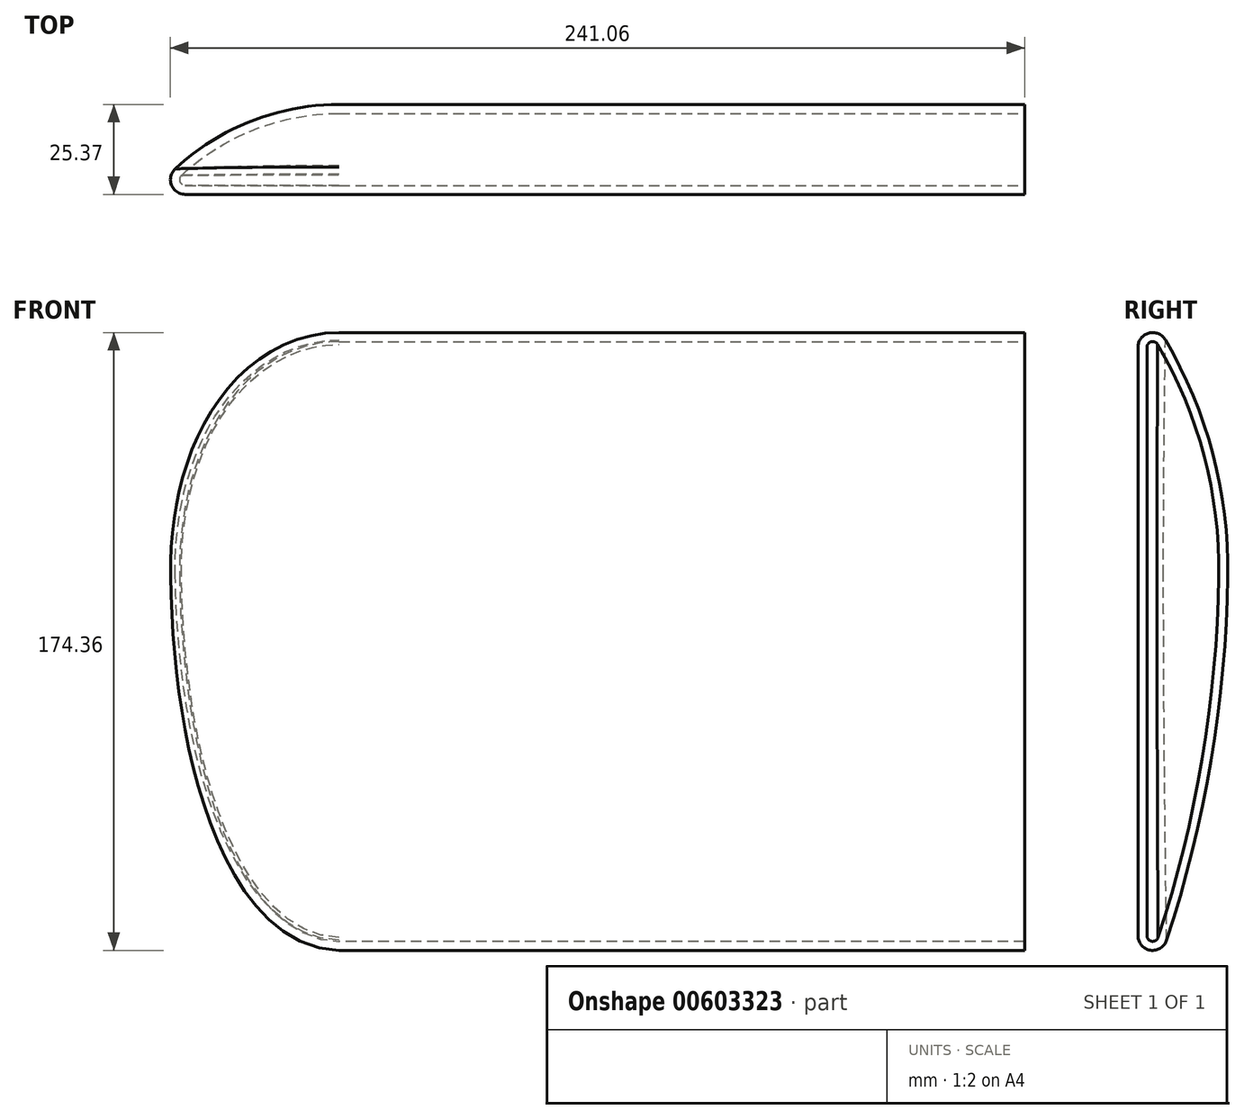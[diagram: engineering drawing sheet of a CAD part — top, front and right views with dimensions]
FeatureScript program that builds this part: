
annotation { "Feature Type Name" : "Feature", "Feature Type Description" : "" }
export const myFeature = defineFeature(function(context is Context, id is Id, definition is map)
    precondition{}
    {
        {
            var Q0;
            Q0=qCreatedBy(makeId("Front.planeOp"),FACE);
            var sketch = newSketch(context, id + "F0", { "sketchPlane" : qUnion([Q0])});
            skLineSegment(sketch, "E0.bottom", {"start": v(35.16, 65.27) * mm, "end": v(-168.9, 65.27) * mm});
            skLineSegment(sketch, "E0.top", {"start": v(35.16, -99.73) * mm, "end": v(-168.9, -99.73) * mm});
            skLineSegment(sketch, "E0.left", {"start": v(35.16, 65.27) * mm, "end": v(35.16, -99.73) * mm});
            skLineSegment(sketch, "E0.right", {"start": v(-168.9, 65.27) * mm, "end": v(-168.9, -99.73) * mm});
            skLineSegment(sketch, "E1.bottom", {"start": v(35.16, 65.27) * mm, "end": v(-226.34, 65.27) * mm});
            skLineSegment(sketch, "E1.top", {"start": v(35.16, -137.93) * mm, "end": v(-226.34, -137.93) * mm});
            skLineSegment(sketch, "E1.left", {"start": v(35.16, 65.27) * mm, "end": v(35.16, -137.93) * mm});
            skLineSegment(sketch, "E1.right", {"start": v(-226.34, 65.27) * mm, "end": v(-226.34, -137.93) * mm});
            skSolve(sketch);
        }
        {
            var Q0;
            {var subQ4=sQuery(id+"F0.wireOp",EDGE,"E0.top");Q0=makeQuery(id+"F0.imprint","IMPRINT",FACE,{"disambiguationData":[TD([[makeQuery(id+"F0.imprint","IMPRINT",EDGE,{"derivedFrom":subQ4}),1.0]])]});}
            extrude(context, id + "F1", {"entities" : qUnion([Q0]), "depth" : 25.4 * mm, "offsetDistance" : 25.4 * mm});
        }
        {
            var Q0;
            Q0=makeQuery(id+"F1.opExtrude","CAP_EDGE",EDGE,{"disambiguationData":[OSD([sQuery(id+"F0.wireOp",EDGE,"E1.bottom")])],"isStart":false});
            fillet(context, id + "F2", {"entities" : qUnion([Q0]), "radius" : 12.88 * mm, "tangentPropagation" : true, "allowEdgeOverflow" : false});
        }
        {
            var Q0;
            Q0=makeQuery(id+"F1.opExtrude","CAP_EDGE",EDGE,{"disambiguationData":[OSD([sQuery(id+"F0.wireOp",EDGE,"E1.bottom")])],"isStart":true});
            fillet(context, id + "F3", {"entities" : qUnion([Q0]), "radius" : 5.08 * mm, "tangentPropagation" : true, "allowEdgeOverflow" : false});
        }
        {
            var Q0;
            Q0=makeQuery(id+"F1.opExtrude","CAP_EDGE",EDGE,{"disambiguationData":[OSD([sQuery(id+"F0.wireOp",EDGE,"E1.right")])],"isStart":true});
            fillet(context, id + "F4", {"entities" : qUnion([Q0]), "radius" : 5.08 * mm, "tangentPropagation" : true, "allowEdgeOverflow" : false});
        }
        {
            var Q0;
            Q0=makeQuery(id+"F1.opExtrude","CAP_EDGE",EDGE,{"disambiguationData":[OSD([sQuery(id+"F0.wireOp",EDGE,"E0.top")])],"isStart":true});
            fillet(context, id + "F5", {"entities" : qUnion([Q0]), "radius" : 5.08 * mm, "tangentPropagation" : true, "allowEdgeOverflow" : false});
        }
        {
            var Q0;
            Q0=makeQuery(id+"F1.opExtrude","CAP_EDGE",EDGE,{"disambiguationData":[OSD([sQuery(id+"F0.wireOp",EDGE,"E0.top")])],"isStart":false});
            fillet(context, id + "F6", {"entities" : qUnion([Q0]), "radius" : 34.95 * mm, "tangentPropagation" : true, "allowEdgeOverflow" : false});
        }
        {
            var Q0;
            Q0 = qSketchRegion(id + "F0", true);
            extrude(context, id + "F7", {"entities" : qUnion([Q0]), "operationType" : NewBodyOperationType.ADD, "depth" : 25.4 * mm, "offsetDistance" : 25.4 * mm});
        }
        {
            var Q0;
            {var subQ0=sQuery(id+"F0.wireOp",EDGE,"E1.top");Q0=makeQuery(id+"F7.boolean.opBoolean","MERGE",EDGE,{"derivedFrom":[makeQuery(id+"F1.opExtrude","CAP_EDGE",EDGE,{"disambiguationData":[OSD([subQ0])],"isStart":true}),makeQuery(id+"F7.opExtrude","CAP_EDGE",EDGE,{"disambiguationData":[OSD([subQ0])],"isStart":true})]});}
            fillet(context, id + "F8", {"entities" : qUnion([Q0]), "radius" : 345.24 * mm, "tangentPropagation" : true, "allowEdgeOverflow" : false});
        }
        {
            var Q0;
            Q0=makeQuery(id+"F7.opExtrude","CAP_EDGE",EDGE,{"disambiguationData":[OSD([sQuery(id+"F0.wireOp",EDGE,"E1.bottom")])],"isStart":true});
            fillet(context, id + "F9", {"entities" : qUnion([Q0]), "radius" : 128.16 * mm, "tangentPropagation" : true, "allowEdgeOverflow" : false});
        }
        {
            var Q0;
            {var subQ0=sQuery(id+"F0.wireOp",EDGE,"E1.right");Q0=makeQuery(id+"F9.opFillet","BLEND_EDGE",EDGE,{"blendedFrom":[makeQuery(id+"F7.opExtrude","CAP_EDGE",EDGE,{"disambiguationData":[OSD([sQuery(id+"F0.wireOp",EDGE,"E1.bottom")])],"isStart":true}),makeQuery(id+"F7.boolean.opBoolean","MERGE",FACE,{"derivedFrom":[makeQuery(id+"F1.opExtrude","SWEPT_FACE",FACE,{"disambiguationData":[OSD([subQ0])]}),makeQuery(id+"F7.opExtrude","SWEPT_FACE",FACE,{"disambiguationData":[OSD([subQ0])]})]})],"blendedInto":[makeQuery(id+"F7.boolean.opBoolean","MERGE",FACE,{"derivedFrom":[makeQuery(id+"F1.opExtrude","SWEPT_FACE",FACE,{"disambiguationData":[OSD([subQ0])]}),makeQuery(id+"F7.opExtrude","SWEPT_FACE",FACE,{"disambiguationData":[OSD([subQ0])]})]})]});}
            fillet(context, id + "F10", {"entities" : qUnion([Q0]), "radius" : 68.07 * mm, "tangentPropagation" : true, "allowEdgeOverflow" : false});
        }
        {
            var Q0;
            {var subQ0=sQuery(id+"F0.wireOp",EDGE,"E1.right");var subQ1=sQuery(id+"F0.wireOp",EDGE,"E1.left");var subQ2=sQuery(id+"F0.wireOp",EDGE,"E1.top");var subQ3=sQuery(id+"F0.wireOp",EDGE,"E1.bottom");Q0=makeQuery(id+"F10.opFillet","BLEND_EDGE",EDGE,{"blendedFrom":[makeQuery(id+"F9.opFillet","BLEND_EDGE",EDGE,{"blendedFrom":[makeQuery(id+"F7.opExtrude","CAP_EDGE",EDGE,{"disambiguationData":[OSD([subQ3])],"isStart":true}),makeQuery(id+"F7.boolean.opBoolean","MERGE",FACE,{"derivedFrom":[makeQuery(id+"F1.opExtrude","SWEPT_FACE",FACE,{"disambiguationData":[OSD([subQ0])]}),makeQuery(id+"F7.opExtrude","SWEPT_FACE",FACE,{"disambiguationData":[OSD([subQ0])]})]})],"blendedInto":[makeQuery(id+"F7.boolean.opBoolean","MERGE",FACE,{"derivedFrom":[makeQuery(id+"F1.opExtrude","SWEPT_FACE",FACE,{"disambiguationData":[OSD([subQ0])]}),makeQuery(id+"F7.opExtrude","SWEPT_FACE",FACE,{"disambiguationData":[OSD([subQ0])]})]})]}),makeQuery(id+"F7.boolean.opBoolean","MERGE",FACE,{"derivedFrom":[makeQuery(id+"F1.opExtrude","CAP_FACE",FACE,{"disambiguationData":[OSD([sQuery(id+"F0.wireOp",EDGE,"E0.top"),sQuery(id+"F0.wireOp",EDGE,"E0.right"),subQ3,subQ2,subQ1,subQ0])],"isStart":false}),makeQuery(id+"F7.opExtrude","CAP_FACE",FACE,{"disambiguationData":[OSD([subQ3,subQ2,subQ1,subQ0])],"isStart":false})]})],"blendedInto":[makeQuery(id+"F7.boolean.opBoolean","MERGE",FACE,{"derivedFrom":[makeQuery(id+"F1.opExtrude","CAP_FACE",FACE,{"disambiguationData":[OSD([sQuery(id+"F0.wireOp",EDGE,"E0.top"),sQuery(id+"F0.wireOp",EDGE,"E0.right"),subQ3,subQ2,subQ1,subQ0])],"isStart":false}),makeQuery(id+"F7.opExtrude","CAP_FACE",FACE,{"disambiguationData":[OSD([subQ3,subQ2,subQ1,subQ0])],"isStart":false})]})]});}
            fillet(context, id + "F11", {"entities" : qUnion([Q0]), "radius" : 4.16 * mm, "tangentPropagation" : true, "allowEdgeOverflow" : false});
        }
        {
            var Q0;
            {var subQ0=sQuery(id+"F0.wireOp",EDGE,"E1.left");Q0=makeQuery(id+"F7.boolean.opBoolean","MERGE",FACE,{"derivedFrom":[makeQuery(id+"F1.opExtrude","SWEPT_FACE",FACE,{"disambiguationData":[OSD([subQ0])]}),makeQuery(id+"F7.opExtrude","SWEPT_FACE",FACE,{"disambiguationData":[OSD([subQ0])]})]});}
            shell(context, id + "F12", {"entities" : qUnion([Q0]), "thickness" : 2.54 * mm});
        }
    });
